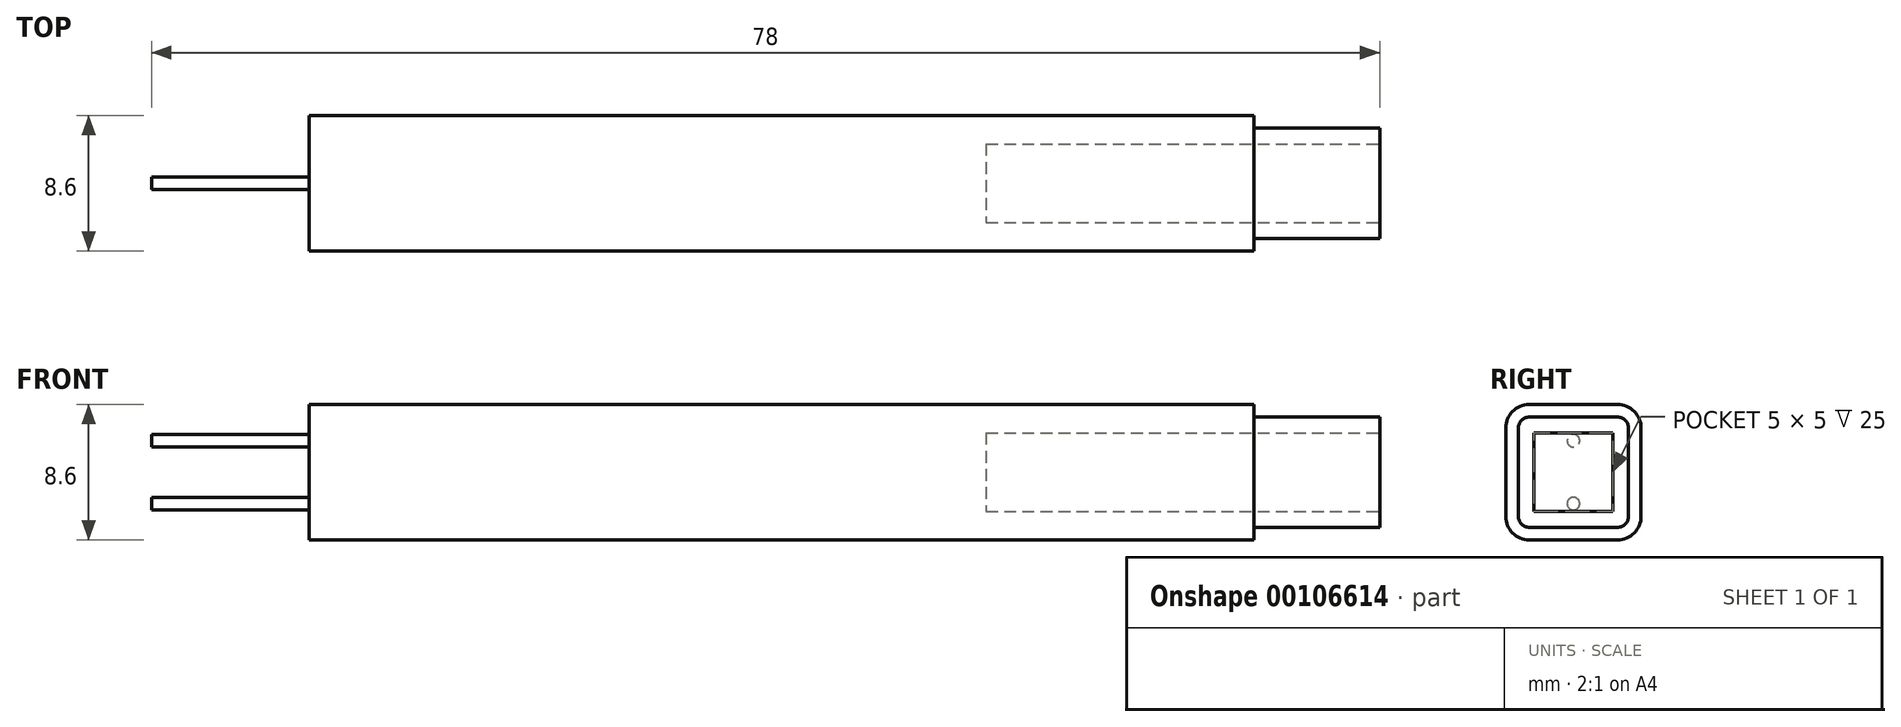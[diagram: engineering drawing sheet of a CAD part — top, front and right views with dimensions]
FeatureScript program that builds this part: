
annotation { "Feature Type Name" : "Feature", "Feature Type Description" : "" }
export const myFeature = defineFeature(function(context is Context, id is Id, definition is map)
    precondition{}
    {
        {
            var Q0;
            Q0=qCreatedBy(makeId("Right.planeOp"),FACE);
            var sketch = newSketch(context, id + "F0", { "sketchPlane" : qUnion([Q0])});
            skLineSegment(sketch, "E0.bottom", {"start": v(2.8, 4.3) * mm, "end": v(-2.8, 4.3) * mm});
            skLineSegment(sketch, "E0.top", {"start": v(2.8, -4.3) * mm, "end": v(-2.8, -4.3) * mm});
            skLineSegment(sketch, "E0.left", {"start": v(4.3, 2.8) * mm, "end": v(4.3, -2.8) * mm});
            skLineSegment(sketch, "E0.right", {"start": v(-4.3, 2.8) * mm, "end": v(-4.3, -2.8) * mm});
            skPoint(sketch, "E1", {"position": v(0, 4.3) * mm});
            skPoint(sketch, "E2", {"position": v(4.3, 0) * mm});
            skPoint(sketch, "E3.visualSharp", {"position": v(4.3, 4.3) * mm});
            skArc(sketch, "E3.filletArc", {"start": v(4.3, 2.8) * mm, "mid": v(3.86, 3.86) * mm, "end": v(2.8, 4.3) * mm});
            skPoint(sketch, "E4.visualSharp", {"position": v(-4.3, 4.3) * mm});
            skArc(sketch, "E4.filletArc", {"start": v(-2.8, 4.3) * mm, "mid": v(-3.86, 3.86) * mm, "end": v(-4.3, 2.8) * mm});
            skPoint(sketch, "E5.visualSharp", {"position": v(-4.3, -4.3) * mm});
            skArc(sketch, "E5.filletArc", {"start": v(-4.3, -2.8) * mm, "mid": v(-3.86, -3.86) * mm, "end": v(-2.8, -4.3) * mm});
            skPoint(sketch, "E6.visualSharp", {"position": v(4.3, -4.3) * mm});
            skArc(sketch, "E6.filletArc", {"start": v(2.8, -4.3) * mm, "mid": v(3.86, -3.86) * mm, "end": v(4.3, -2.8) * mm});
            skSolve(sketch);
        }
        {
            var Q0;
            Q0 = qSketchRegion(id + "F0", true);
            extrude(context, id + "F1", {"entities" : qUnion([Q0]), "depth" : 60 * mm});
        }
        {
            var Q0;
            Q0=makeQuery(id+"F1.opExtrude","CAP_FACE",FACE,{"disambiguationData":[OSD([sQuery(id+"F0.wireOp",EDGE,"E0.bottom"),sQuery(id+"F0.wireOp",EDGE,"E0.top"),sQuery(id+"F0.wireOp",EDGE,"E0.left"),sQuery(id+"F0.wireOp",EDGE,"E0.right"),sQuery(id+"F0.wireOp",EDGE,"E3.filletArc"),sQuery(id+"F0.wireOp",EDGE,"E4.filletArc"),sQuery(id+"F0.wireOp",EDGE,"E5.filletArc"),sQuery(id+"F0.wireOp",EDGE,"E6.filletArc")])],"isStart":false});
            var sketch = newSketch(context, id + "F2", { "sketchPlane" : qUnion([Q0])});
            skArc(sketch, "E7.0", {"start": v(-2.8, 3.5) * mm, "mid": v(-3.3, 3.3) * mm, "end": v(-3.5, 2.8) * mm});
            skLineSegment(sketch, "E7.1", {"start": v(2.8, 3.5) * mm, "end": v(-2.8, 3.5) * mm});
            skLineSegment(sketch, "E7.2", {"start": v(-3.5, 2.8) * mm, "end": v(-3.5, -2.8) * mm});
            skArc(sketch, "E7.3", {"start": v(3.5, 2.8) * mm, "mid": v(3.3, 3.3) * mm, "end": v(2.8, 3.5) * mm});
            skArc(sketch, "E7.4", {"start": v(-3.5, -2.8) * mm, "mid": v(-3.3, -3.3) * mm, "end": v(-2.8, -3.5) * mm});
            skLineSegment(sketch, "E7.5", {"start": v(2.8, -3.5) * mm, "end": v(-2.8, -3.5) * mm});
            skArc(sketch, "E7.6", {"start": v(2.8, -3.5) * mm, "mid": v(3.3, -3.3) * mm, "end": v(3.5, -2.8) * mm});
            skLineSegment(sketch, "E7.7", {"start": v(3.5, 2.8) * mm, "end": v(3.5, -2.8) * mm});
            skSolve(sketch);
        }
        {
            var Q0;
            Q0 = qSketchRegion(id + "F2", true);
            extrude(context, id + "F3", {"entities" : qUnion([Q0]), "operationType" : NewBodyOperationType.ADD, "depth" : 8 * mm});
        }
        {
            var Q0;
            Q0=makeQuery(id+"F1.opExtrude","CAP_FACE",FACE,{"disambiguationData":[OSD([sQuery(id+"F0.wireOp",EDGE,"E0.bottom"),sQuery(id+"F0.wireOp",EDGE,"E0.top"),sQuery(id+"F0.wireOp",EDGE,"E0.left"),sQuery(id+"F0.wireOp",EDGE,"E0.right"),sQuery(id+"F0.wireOp",EDGE,"E3.filletArc"),sQuery(id+"F0.wireOp",EDGE,"E4.filletArc"),sQuery(id+"F0.wireOp",EDGE,"E5.filletArc"),sQuery(id+"F0.wireOp",EDGE,"E6.filletArc")])],"isStart":true});
            var sketch = newSketch(context, id + "F4", { "sketchPlane" : qUnion([Q0])});
            skCircle(sketch, "E8", {"center": v(0, 2) * mm, "radius": 0.4 * mm});
            skCircle(sketch, "E9", {"center": v(0, -2) * mm, "radius": 0.4 * mm});
            skSolve(sketch);
        }
        {
            var Q0;
            Q0 = qSketchRegion(id + "F4", true);
            extrude(context, id + "F5", {"entities" : qUnion([Q0]), "operationType" : NewBodyOperationType.ADD, "depth" : 10 * mm});
        }
        {
            var Q0;
            Q0=makeQuery(id+"F3.opExtrude","CAP_FACE",FACE,{"disambiguationData":[OSD([sQuery(id+"F2.wireOp",EDGE,"E7.0"),sQuery(id+"F2.wireOp",EDGE,"E7.1"),sQuery(id+"F2.wireOp",EDGE,"E7.2"),sQuery(id+"F2.wireOp",EDGE,"E7.3"),sQuery(id+"F2.wireOp",EDGE,"E7.4"),sQuery(id+"F2.wireOp",EDGE,"E7.5"),sQuery(id+"F2.wireOp",EDGE,"E7.6"),sQuery(id+"F2.wireOp",EDGE,"E7.7")])],"isStart":false});
            var sketch = newSketch(context, id + "F6", { "sketchPlane" : qUnion([Q0])});
            skLineSegment(sketch, "E10.0", {"start": v(2.5, 2.5) * mm, "end": v(-2.5, 2.5) * mm});
            skLineSegment(sketch, "E10.1", {"start": v(2.5, 2.5) * mm, "end": v(2.5, -2.5) * mm});
            skLineSegment(sketch, "E10.2", {"start": v(2.5, -2.5) * mm, "end": v(-2.5, -2.5) * mm});
            skLineSegment(sketch, "E10.3", {"start": v(-2.5, 2.5) * mm, "end": v(-2.5, -2.5) * mm});
            skSolve(sketch);
        }
        {
            var Q0;
            Q0 = qSketchRegion(id + "F6", true);
            extrude(context, id + "F7", {"entities" : qUnion([Q0]), "operationType" : NewBodyOperationType.REMOVE, "oppositeDirection" : true, "depth" : 25 * mm});
        }
    });
